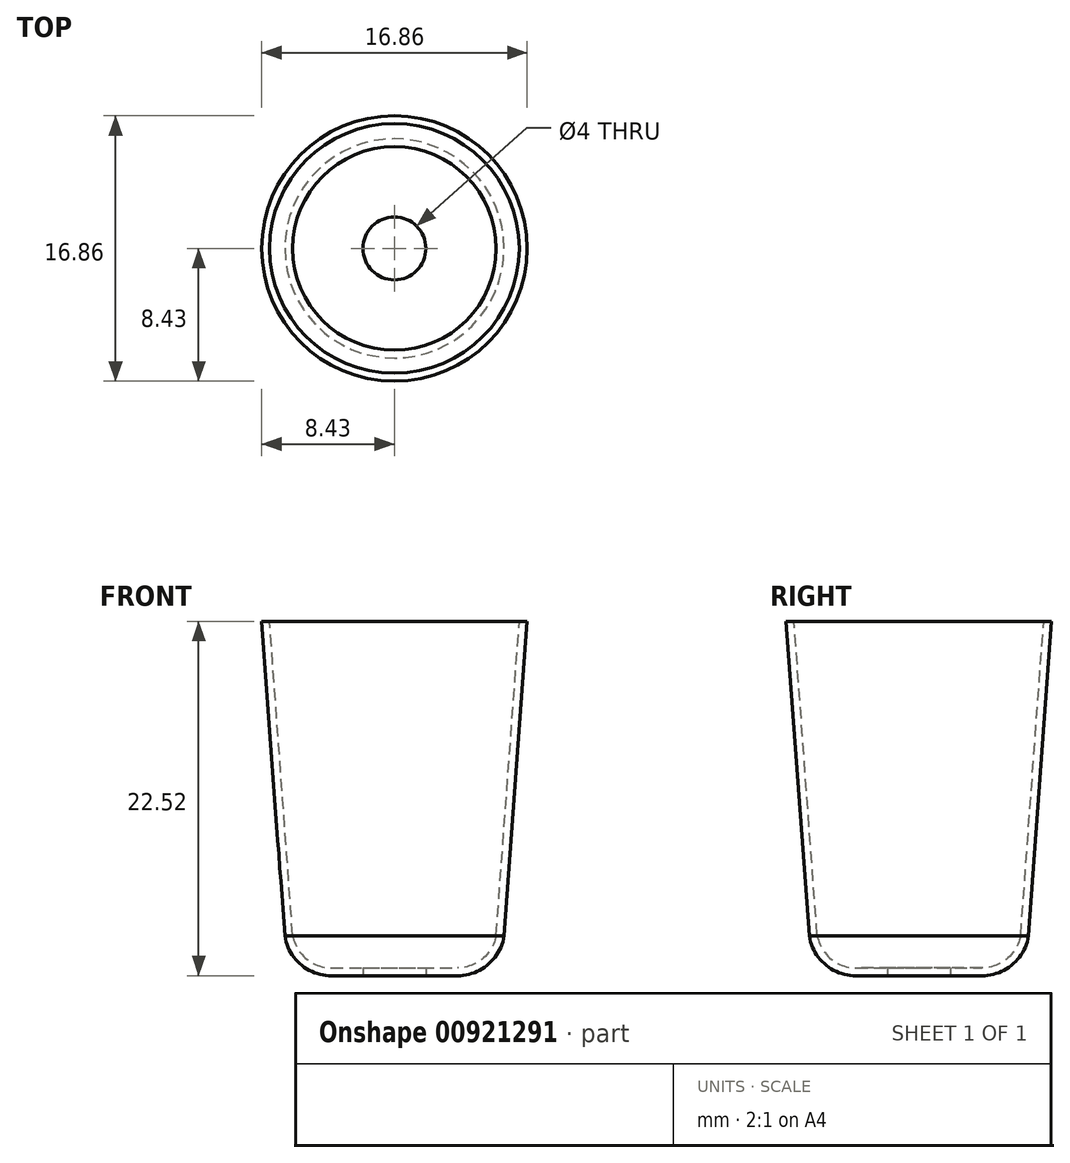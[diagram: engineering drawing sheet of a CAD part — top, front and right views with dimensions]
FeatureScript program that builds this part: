
annotation { "Feature Type Name" : "Feature", "Feature Type Description" : "" }
export const myFeature = defineFeature(function(context is Context, id is Id, definition is map)
    precondition{}
    {
        {
            var Q0;
            Q0=qCreatedBy(makeId("Front.planeOp"),FACE);
            var sketch = newSketch(context, id + "F0", { "sketchPlane" : qUnion([Q0])});
            skLineSegment(sketch, "E0", {"start": v(2, 0) * mm, "end": v(4, 0) * mm});
            skArc(sketch, "E1", {"start": v(4, 0) * mm, "mid": v(5.94, 0.72) * mm, "end": v(6.96, 2.52) * mm});
            skLineSegment(sketch, "E2", {"start": v(6.96, 2.52) * mm, "end": v(8.43, 22.52) * mm});
            skLineSegment(sketch, "E3", {"start": v(0, 0) * mm, "end": v(0, 20) * mm, "construction": true});
            skLineSegment(sketch, "E4.0", {"start": v(6.46, 2.58) * mm, "end": v(7.93, 22.52) * mm});
            skArc(sketch, "E4.1", {"start": v(4, 0.5) * mm, "mid": v(5.61, 1.09) * mm, "end": v(6.46, 2.58) * mm});
            skLineSegment(sketch, "E4.2", {"start": v(2, 0.5) * mm, "end": v(4, 0.5) * mm});
            skLineSegment(sketch, "E5", {"start": v(8.43, 22.52) * mm, "end": v(7.93, 22.52) * mm});
            skLineSegment(sketch, "E6", {"start": v(2, 0) * mm, "end": v(2, 0.5) * mm});
            skSolve(sketch);
        }
        {
            var Q0;
            Q0=makeQuery(id+"F0.imprint","IMPRINT",FACE,{"disambiguationData":[TD([[makeQuery(id+"F0.imprint","IMPRINT",EDGE,{"derivedFrom":sQuery(id+"F0.wireOp",EDGE,"E0")}),1.0]])]});
            var Q1;
            Q1=sQuery(id+"F0.wireOp",EDGE,"E3");
            revolve(context, id + "F1", {"surfaceOperationType" : NewSurfaceOperationType.NEW, "entities" : qUnion([Q0]), "axis" : qUnion([Q1]), "revolveType" : RevolveType.FULL});
        }
    });
